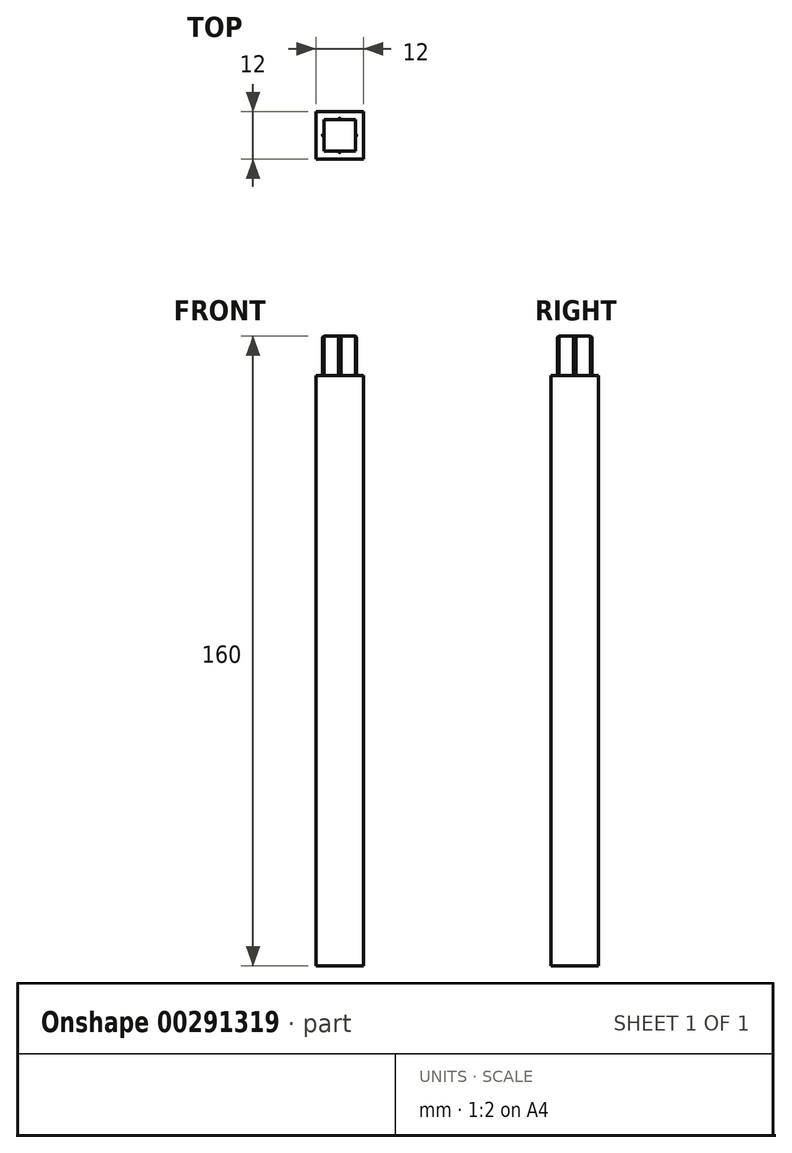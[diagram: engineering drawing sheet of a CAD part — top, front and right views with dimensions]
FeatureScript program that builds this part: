
annotation { "Feature Type Name" : "Feature", "Feature Type Description" : "" }
export const myFeature = defineFeature(function(context is Context, id is Id, definition is map)
    precondition{}
    {
        {
            var Q0;
            Q0=qCreatedBy(makeId("Top.planeOp"),FACE);
            var sketch = newSketch(context, id + "F0", { "sketchPlane" : qUnion([Q0])});
            skLineSegment(sketch, "E0.bottom", {"start": v(-6, 6) * mm, "end": v(6, 6) * mm});
            skLineSegment(sketch, "E0.top", {"start": v(-6, -6) * mm, "end": v(6, -6) * mm});
            skLineSegment(sketch, "E0.left", {"start": v(-6, 6) * mm, "end": v(-6, -6) * mm});
            skLineSegment(sketch, "E0.right", {"start": v(6, 6) * mm, "end": v(6, -6) * mm});
            skPoint(sketch, "E0.middle", {"position": v(0, 0) * mm});
            skSolve(sketch);
        }
        {
            var Q0;
            Q0=makeQuery(id+"F0.imprint","IMPRINT",FACE,{"disambiguationData":[TD([[makeQuery(id+"F0.imprint","IMPRINT",EDGE,{"derivedFrom":sQuery(id+"F0.wireOp",EDGE,"E0.bottom")}),-1.0]])]});
            extrude(context, id + "F1", {"entities" : qUnion([Q0]), "endBound" : BoundingType.SYMMETRIC, "depth" : 150 * mm});
        }
        {
            var Q0;
            Q0=makeQuery(id+"F1.opExtrude","CAP_FACE",FACE,{"disambiguationData":[OSD([sQuery(id+"F0.wireOp",EDGE,"E0.bottom"),sQuery(id+"F0.wireOp",EDGE,"E0.top"),sQuery(id+"F0.wireOp",EDGE,"E0.left"),sQuery(id+"F0.wireOp",EDGE,"E0.right")])],"isStart":false});
            var sketch = newSketch(context, id + "F2", { "sketchPlane" : qUnion([Q0])});
            skLineSegment(sketch, "E1.bottom", {"start": v(-4.33, 4.33) * mm, "end": v(4.33, 4.33) * mm, "construction": true});
            skLineSegment(sketch, "E1.top", {"start": v(-4.33, -4.33) * mm, "end": v(4.33, -4.33) * mm, "construction": true});
            skLineSegment(sketch, "E1.left", {"start": v(-4.33, 4.33) * mm, "end": v(-4.33, -4.33) * mm, "construction": true});
            skLineSegment(sketch, "E1.right", {"start": v(4.33, 4.33) * mm, "end": v(4.33, -4.33) * mm, "construction": true});
            skPoint(sketch, "E1.middle", {"position": v(0, 0) * mm});
            skLineSegment(sketch, "E2.bottom", {"start": v(-4, 4) * mm, "end": v(4, 4) * mm});
            skLineSegment(sketch, "E2.top", {"start": v(-4, -4) * mm, "end": v(4, -4) * mm});
            skLineSegment(sketch, "E2.left", {"start": v(-4, 4) * mm, "end": v(-4, -4) * mm});
            skLineSegment(sketch, "E2.right", {"start": v(4, 4) * mm, "end": v(4, -4) * mm});
            skArc(sketch, "E3", {"start": v(0.33, 4) * mm, "mid": v(0, 4.33) * mm, "end": v(-0.33, 4) * mm});
            skArc(sketch, "E4", {"start": v(4, -0.33) * mm, "mid": v(4.33, 0) * mm, "end": v(4, 0.33) * mm});
            skArc(sketch, "E5", {"start": v(0.33, -4) * mm, "mid": v(0, -4.33) * mm, "end": v(-0.33, -4) * mm});
            skArc(sketch, "E6", {"start": v(-4, 0.32) * mm, "mid": v(-4.33, 0) * mm, "end": v(-4, -0.32) * mm});
            skSolve(sketch);
        }
        {
            var Q0;
            Q0 = qSketchRegion(id + "F2", true);
            extrude(context, id + "F3", {"entities" : qUnion([Q0]), "operationType" : NewBodyOperationType.ADD, "depth" : 10 * mm});
        }
        {
            var Q0;
            Q0=makeQuery(id+"F3.opExtrude","CAP_EDGE",EDGE,{"disambiguationData":[OSD([sQuery(id+"F2.wireOp",EDGE,"E5")])],"isStart":false});
            var Q1;
            Q1=makeQuery(id+"F3.opExtrude","CAP_EDGE",EDGE,{"disambiguationData":[OSD([sQuery(id+"F2.wireOp",EDGE,"E4")])],"isStart":false});
            var Q2;
            Q2=makeQuery(id+"F3.opExtrude","CAP_EDGE",EDGE,{"disambiguationData":[OSD([sQuery(id+"F2.wireOp",EDGE,"E3")])],"isStart":false});
            var Q3;
            Q3=makeQuery(id+"F3.opExtrude","CAP_EDGE",EDGE,{"disambiguationData":[OSD([sQuery(id+"F2.wireOp",EDGE,"E6")])],"isStart":false});
            chamfer(context, id + "F4", {"entities" : qUnion([Q0, Q1, Q2, Q3]), "width" : .3 * mm, "tangentPropagation" : true});
        }
    });
